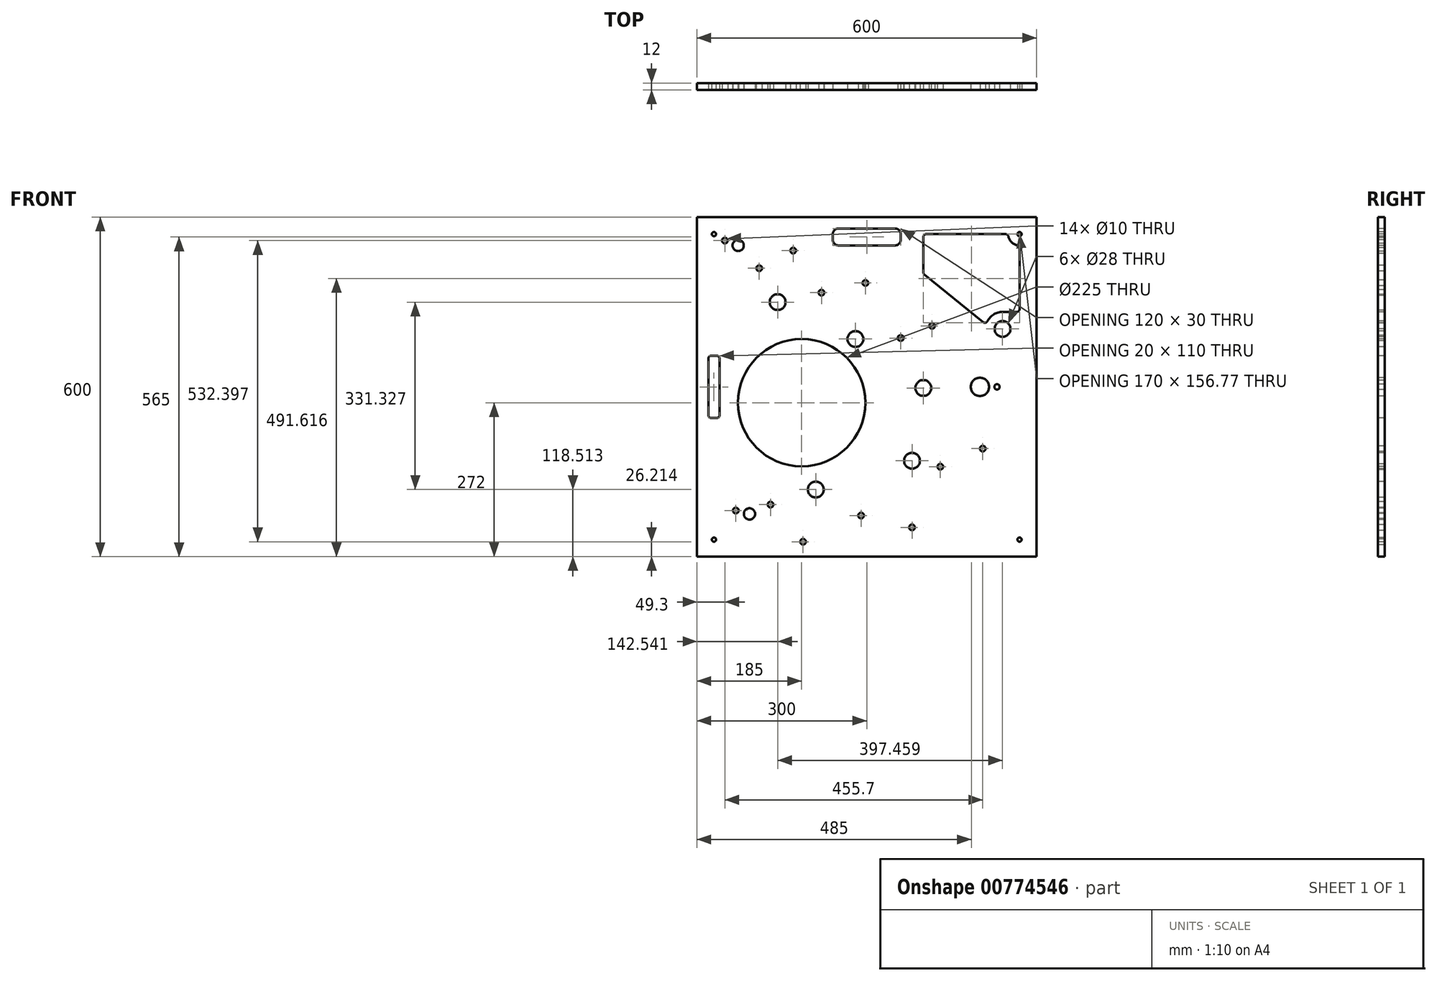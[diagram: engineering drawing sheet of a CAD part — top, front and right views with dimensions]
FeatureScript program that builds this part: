
annotation { "Feature Type Name" : "Feature", "Feature Type Description" : "" }
export const myFeature = defineFeature(function(context is Context, id is Id, definition is map)
    precondition{}
    {
        {
            var Q0;
            Q0=qCreatedBy(makeId("Front.planeOp"),FACE);
            var sketch = newSketch(context, id + "F0", { "sketchPlane" : qUnion([Q0])});
            skLineSegment(sketch, "E0.bottom", {"start": v(0, 0) * mm, "end": v(600, 0) * mm});
            skLineSegment(sketch, "E0.top", {"start": v(0, 600) * mm, "end": v(600, 600) * mm});
            skLineSegment(sketch, "E0.left", {"start": v(0, 0) * mm, "end": v(0, 600) * mm});
            skLineSegment(sketch, "E0.right", {"start": v(600, 0) * mm, "end": v(600, 600) * mm});
            skArc(sketch, "E1", {"start": v(189.89, 51.35) * mm, "mid": v(406.46, 98.95) * mm, "end": v(500, 300) * mm, "construction": true});
            skLineSegment(sketch, "E2", {"start": v(189.89, 51.35) * mm, "end": v(92.83, 75.42) * mm, "construction": true});
            skArc(sketch, "E3", {"start": v(500, 300) * mm, "mid": v(345.36, 426.39) * mm, "end": v(166.65, 515.56) * mm, "construction": true});
            skCircle(sketch, "E4", {"center": v(500, 300) * mm, "radius": 16.15 * mm});
            skCircle(sketch, "E5", {"center": v(530.2, 300) * mm, "radius": 4.68 * mm});
            skLineSegment(sketch, "E6", {"start": v(500, 300) * mm, "end": v(530.2, 300) * mm});
            skLineSegment(sketch, "E7", {"start": v(166.65, 515.56) * mm, "end": v(72.77, 550) * mm, "construction": true});
            skCircle(sketch, "E8", {"center": v(297.76, 483.68) * mm, "radius": 5 * mm});
            skCircle(sketch, "E9", {"center": v(415.4, 407.8) * mm, "radius": 5 * mm});
            skCircle(sketch, "E10", {"center": v(170, 540.94) * mm, "radius": 5 * mm});
            skCircle(sketch, "E11", {"center": v(430, 158.9) * mm, "radius": 5 * mm});
            skCircle(sketch, "E12", {"center": v(360, 386.36) * mm, "radius": 5 * mm});
            skCircle(sketch, "E13", {"center": v(220, 466.62) * mm, "radius": 5 * mm});
            skCircle(sketch, "E14", {"center": v(72.77, 550) * mm, "radius": 10 * mm});
            skCircle(sketch, "E15", {"center": v(49.3, 558.61) * mm, "radius": 15 * mm, "construction": true});
            skCircle(sketch, "E16", {"center": v(380, 51.62) * mm, "radius": 5 * mm});
            skCircle(sketch, "E17", {"center": v(505, 190.86) * mm, "radius": 5 * mm});
            skCircle(sketch, "E18", {"center": v(187.48, 26.21) * mm, "radius": 5 * mm});
            skPoint(sketch, "E19.centerSnap0", {"position": v(406.46, 98.95) * mm});
            skArc(sketch, "E20.1", {"start": v(509.87, 304.2) * mm, "mid": v(352.43, 433.72) * mm, "end": v(170.1, 524.94) * mm, "construction": true});
            skArc(sketch, "E20.2", {"start": v(187.48, 41.64) * mm, "mid": v(414.26, 92.4) * mm, "end": v(509.87, 304.2) * mm, "construction": true});
            skLineSegment(sketch, "E20.3", {"start": v(187.48, 41.64) * mm, "end": v(77.4, 68.95) * mm, "construction": true});
            skLineSegment(sketch, "E21.0", {"start": v(163.2, 506.17) * mm, "end": v(35.36, 553.07) * mm, "construction": true});
            skArc(sketch, "E21.1", {"start": v(490.07, 295.84) * mm, "mid": v(338.26, 419.07) * mm, "end": v(163.2, 506.17) * mm, "construction": true});
            skArc(sketch, "E21.2", {"start": v(192.3, 61.05) * mm, "mid": v(398.67, 105.53) * mm, "end": v(490.07, 295.84) * mm, "construction": true});
            skLineSegment(sketch, "E21.3", {"start": v(192.3, 61.05) * mm, "end": v(85.57, 87.53) * mm, "construction": true});
            skCircle(sketch, "E22", {"center": v(297.76, 483.68) * mm, "radius": 15 * mm, "construction": true});
            skCircle(sketch, "E23", {"center": v(415.4, 407.8) * mm, "radius": 15 * mm, "construction": true});
            skLineSegment(sketch, "E24.0", {"start": v(170.1, 524.94) * mm, "end": v(42.25, 571.85) * mm, "construction": true});
            skCircle(sketch, "E25", {"center": v(280, 384.55) * mm, "radius": 14 * mm});
            skCircle(sketch, "E26", {"center": v(570, 570) * mm, "radius": 3.75 * mm});
            skCircle(sketch, "E27", {"center": v(400, 298.07) * mm, "radius": 14 * mm});
            skArc(sketch, "E28.0", {"start": v(428.72, 272) * mm, "mid": v(294.75, 375.6) * mm, "end": v(142.54, 449.84) * mm, "construction": true});
            skLineSegment(sketch, "E29.bottom", {"start": v(350, 580) * mm, "end": v(250, 580) * mm});
            skLineSegment(sketch, "E29.top", {"start": v(350, 550) * mm, "end": v(250, 550) * mm});
            skLineSegment(sketch, "E29.left", {"start": v(360, 570) * mm, "end": v(360, 560) * mm});
            skLineSegment(sketch, "E29.right", {"start": v(240, 570) * mm, "end": v(240, 560) * mm});
            skPoint(sketch, "E30.visualSharp", {"position": v(240, 580) * mm});
            skArc(sketch, "E30.filletArc", {"start": v(250, 580) * mm, "mid": v(242.93, 577.07) * mm, "end": v(240, 570) * mm});
            skPoint(sketch, "E31.visualSharp", {"position": v(240, 550) * mm});
            skArc(sketch, "E31.filletArc", {"start": v(240, 560) * mm, "mid": v(242.93, 552.93) * mm, "end": v(250, 550) * mm});
            skPoint(sketch, "E32.visualSharp", {"position": v(360, 550) * mm});
            skArc(sketch, "E32.filletArc", {"start": v(350, 550) * mm, "mid": v(357.07, 552.93) * mm, "end": v(360, 560) * mm});
            skPoint(sketch, "E33.visualSharp", {"position": v(360, 580) * mm});
            skArc(sketch, "E33.filletArc", {"start": v(360, 570) * mm, "mid": v(357.07, 577.07) * mm, "end": v(350, 580) * mm});
            skLineSegment(sketch, "E34", {"start": v(300, 600) * mm, "end": v(300, 580) * mm, "construction": true});
            skCircle(sketch, "E35", {"center": v(170, 540.94) * mm, "radius": 15 * mm, "construction": true});
            skCircle(sketch, "E36", {"center": v(220, 466.62) * mm, "radius": 15 * mm, "construction": true});
            skCircle(sketch, "E37", {"center": v(360, 386.36) * mm, "radius": 15 * mm, "construction": true});
            skLineSegment(sketch, "E38", {"start": v(170.1, 524.94) * mm, "end": v(142.54, 449.84) * mm, "construction": true});
            skCircle(sketch, "E39", {"center": v(142.54, 449.84) * mm, "radius": 14 * mm});
            skArc(sketch, "E40.0", {"start": v(210, 118.51) * mm, "mid": v(353.46, 146.65) * mm, "end": v(428.72, 272) * mm, "construction": true});
            skCircle(sketch, "E41", {"center": v(380, 169.42) * mm, "radius": 14 * mm});
            skCircle(sketch, "E42", {"center": v(210, 118.51) * mm, "radius": 14 * mm});
            skCircle(sketch, "E43", {"center": v(505, 190.86) * mm, "radius": 15 * mm, "construction": true});
            skCircle(sketch, "E44", {"center": v(380, 51.62) * mm, "radius": 15 * mm, "construction": true});
            skCircle(sketch, "E45", {"center": v(187.48, 26.21) * mm, "radius": 15 * mm, "construction": true});
            skCircle(sketch, "E46", {"center": v(92.83, 75.42) * mm, "radius": 10 * mm});
            skLineSegment(sketch, "E47", {"start": v(72.77, 550) * mm, "end": v(49.3, 558.61) * mm, "construction": true});
            skCircle(sketch, "E48", {"center": v(49.3, 558.61) * mm, "radius": 5 * mm});
            skLineSegment(sketch, "E49.bottom", {"start": v(25, 355) * mm, "end": v(35, 355) * mm});
            skLineSegment(sketch, "E49.top", {"start": v(25, 245) * mm, "end": v(35, 245) * mm});
            skLineSegment(sketch, "E49.left", {"start": v(20, 350) * mm, "end": v(20, 250) * mm});
            skLineSegment(sketch, "E49.right", {"start": v(40, 350) * mm, "end": v(40, 250) * mm});
            skPoint(sketch, "E50.visualSharp", {"position": v(20, 355) * mm});
            skArc(sketch, "E50.filletArc", {"start": v(25, 355) * mm, "mid": v(21.46, 353.54) * mm, "end": v(20, 350) * mm});
            skPoint(sketch, "E51.visualSharp", {"position": v(40, 245) * mm});
            skArc(sketch, "E51.filletArc", {"start": v(35, 245) * mm, "mid": v(38.54, 246.46) * mm, "end": v(40, 250) * mm});
            skPoint(sketch, "E52.visualSharp", {"position": v(20, 245) * mm});
            skArc(sketch, "E52.filletArc", {"start": v(20, 250) * mm, "mid": v(21.46, 246.46) * mm, "end": v(25, 245) * mm});
            skLineSegment(sketch, "E53", {"start": v(0, 300) * mm, "end": v(20, 300) * mm, "construction": true});
            skPoint(sketch, "E54.visualSharp", {"position": v(40, 355) * mm});
            skArc(sketch, "E54.filletArc", {"start": v(40, 350) * mm, "mid": v(38.54, 353.54) * mm, "end": v(35, 355) * mm});
            skLineSegment(sketch, "E55", {"start": v(92.83, 75.42) * mm, "end": v(68.56, 81.44) * mm, "construction": true});
            skCircle(sketch, "E56", {"center": v(68.56, 81.44) * mm, "radius": 15 * mm, "construction": true});
            skCircle(sketch, "E57", {"center": v(68.56, 81.44) * mm, "radius": 5 * mm});
            skCircle(sketch, "E58", {"center": v(430, 158.9) * mm, "radius": 15 * mm, "construction": true});
            skCircle(sketch, "E59", {"center": v(290, 72.57) * mm, "radius": 5 * mm});
            skCircle(sketch, "E60", {"center": v(290, 72.57) * mm, "radius": 15 * mm, "construction": true});
            skCircle(sketch, "E61.MirrorC", {"center": v(30, 570) * mm, "radius": 3.75 * mm});
            skCircle(sketch, "E62.MirrorC", {"center": v(570, 30) * mm, "radius": 3.75 * mm});
            skCircle(sketch, "E63.MirrorC", {"center": v(30, 30) * mm, "radius": 3.75 * mm});
            skCircle(sketch, "E64", {"center": v(185, 272) * mm, "radius": 112.5 * mm});
            skCircle(sketch, "E65", {"center": v(540, 402.47) * mm, "radius": 14 * mm});
            skCircle(sketch, "E66", {"center": v(110, 509.71) * mm, "radius": 5 * mm});
            skCircle(sketch, "E67", {"center": v(110, 509.71) * mm, "radius": 15 * mm, "construction": true});
            skArc(sketch, "E68", {"start": v(550.4, 566) * mm, "mid": v(555.86, 555.86) * mm, "end": v(566, 550.4) * mm});
            skLineSegment(sketch, "E69", {"start": v(545.5, 570) * mm, "end": v(405, 570) * mm});
            skLineSegment(sketch, "E70", {"start": v(400, 565) * mm, "end": v(400, 502.38) * mm});
            skLineSegment(sketch, "E71", {"start": v(401.85, 498.5) * mm, "end": v(505.6, 414.35) * mm});
            skArc(sketch, "E72", {"start": v(540, 432.47) * mm, "mid": v(524.27, 428.02) * mm, "end": v(513.21, 415.98) * mm});
            skLineSegment(sketch, "E73", {"start": v(570, 545.5) * mm, "end": v(570, 437.47) * mm});
            skLineSegment(sketch, "E74", {"start": v(565, 432.47) * mm, "end": v(540, 432.47) * mm});
            skPoint(sketch, "E75.visualSharp", {"position": v(400, 570) * mm});
            skArc(sketch, "E75.filletArc", {"start": v(405, 570) * mm, "mid": v(401.46, 568.54) * mm, "end": v(400, 565) * mm});
            skPoint(sketch, "E76.visualSharp", {"position": v(550, 570) * mm});
            skArc(sketch, "E76.filletArc", {"start": v(550.4, 566) * mm, "mid": v(548.67, 568.87) * mm, "end": v(545.5, 570) * mm});
            skPoint(sketch, "E77.visualSharp", {"position": v(570, 550) * mm});
            skArc(sketch, "E77.filletArc", {"start": v(570, 545.5) * mm, "mid": v(568.87, 548.67) * mm, "end": v(566, 550.4) * mm});
            skPoint(sketch, "E78.visualSharp", {"position": v(570, 432.47) * mm});
            skArc(sketch, "E78.filletArc", {"start": v(565, 432.47) * mm, "mid": v(568.54, 433.93) * mm, "end": v(570, 437.47) * mm});
            skPoint(sketch, "E79.visualSharp", {"position": v(510.96, 410) * mm});
            skArc(sketch, "E79.filletArc", {"start": v(505.6, 414.35) * mm, "mid": v(509.8, 413.34) * mm, "end": v(513.21, 415.98) * mm});
            skPoint(sketch, "E80.visualSharp", {"position": v(400, 500) * mm});
            skArc(sketch, "E80.filletArc", {"start": v(400, 502.38) * mm, "mid": v(400.49, 500.23) * mm, "end": v(401.85, 498.5) * mm});
            skArc(sketch, "E81.trimOffspring", {"start": v(99.22, 550.95) * mm, "mid": v(87.55, 545.1) * mm, "end": v(76.65, 537.92) * mm, "construction": true});
            skArc(sketch, "E82.trimOffspring", {"start": v(176.44, 554.48) * mm, "mid": v(174.29, 555.16) * mm, "end": v(172.12, 555.79) * mm, "construction": true});
            skArc(sketch, "E83.trimOffspring", {"start": v(250.94, 468.52) * mm, "mid": v(247.8, 481.77) * mm, "end": v(243.06, 494.52) * mm, "construction": true});
            skCircle(sketch, "E84", {"center": v(130, 91.96) * mm, "radius": 15 * mm, "construction": true});
            skCircle(sketch, "E85", {"center": v(130, 91.96) * mm, "radius": 5 * mm});
            skSolve(sketch);
        }
        {
            var Q0;
            Q0=makeQuery(id+"F0.imprint","IMPRINT",FACE,{"disambiguationData":[TD([[makeQuery(id+"F0.imprint","IMPRINT",EDGE,{"derivedFrom":sQuery(id+"F0.wireOp",EDGE,"E0.bottom")}),1.0]])]});
            extrude(context, id + "F1", {"entities" : qUnion([Q0]), "oppositeDirection" : true, "depth" : 12 * mm, "offsetDistance" : 25 * mm});
        }
    });
